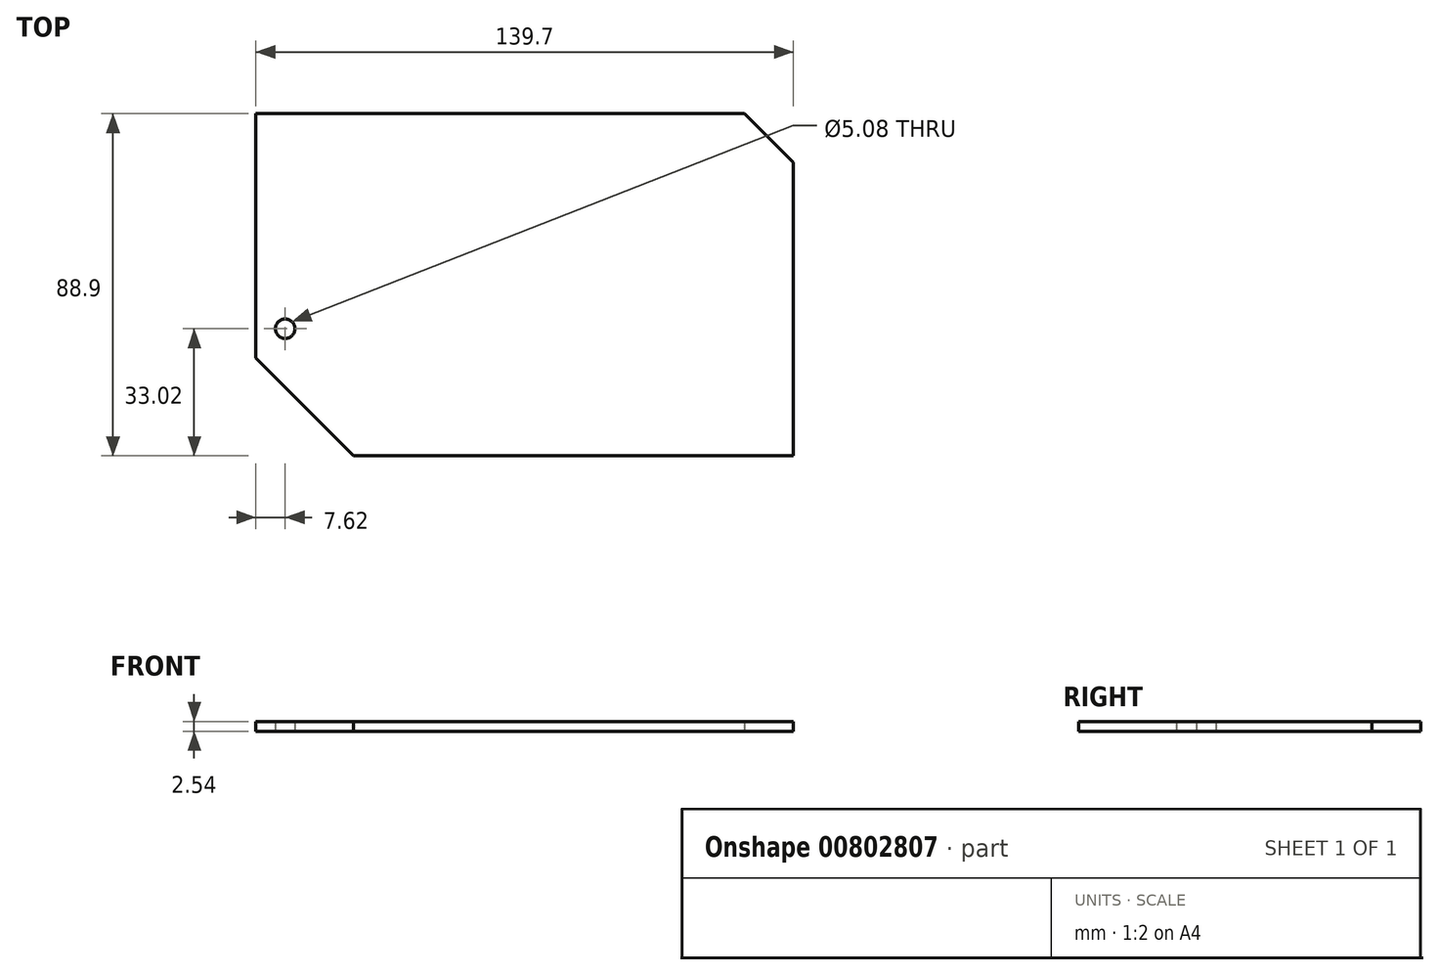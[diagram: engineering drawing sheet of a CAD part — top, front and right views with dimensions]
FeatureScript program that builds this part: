
annotation { "Feature Type Name" : "Feature", "Feature Type Description" : "" }
export const myFeature = defineFeature(function(context is Context, id is Id, definition is map)
    precondition{}
    {
        {
            var Q0;
            Q0=qCreatedBy(makeId("Top.planeOp"),FACE);
            var sketch = newSketch(context, id + "F0", { "sketchPlane" : qUnion([Q0])});
            skLineSegment(sketch, "E0", {"start": v(0, 0) * mm, "end": v(-114.3, 0) * mm});
            skLineSegment(sketch, "E1", {"start": v(-114.3, 0) * mm, "end": v(-139.7, 25.4) * mm});
            skLineSegment(sketch, "E2", {"start": v(-139.7, 25.4) * mm, "end": v(-139.7, 88.9) * mm});
            skLineSegment(sketch, "E3", {"start": v(-139.7, 88.9) * mm, "end": v(-12.7, 88.9) * mm});
            skLineSegment(sketch, "E4", {"start": v(-12.7, 88.9) * mm, "end": v(0, 76.2) * mm});
            skLineSegment(sketch, "E5", {"start": v(0, 76.2) * mm, "end": v(0, 0) * mm});
            skCircle(sketch, "E6", {"center": v(-132.08, 33.02) * mm, "radius": 2.54 * mm});
            skSolve(sketch);
        }
        {
            var Q0;
            Q0=makeQuery(id+"F0.imprint","IMPRINT",FACE,{"disambiguationData":[TD([[makeQuery(id+"F0.imprint","IMPRINT",EDGE,{"derivedFrom":sQuery(id+"F0.wireOp",EDGE,"E0")}),-1.0]])]});
            extrude(context, id + "F1", {"entities" : qUnion([Q0]), "depth" : 2.54 * mm, "offsetDistance" : 25.4 * mm});
        }
    });
